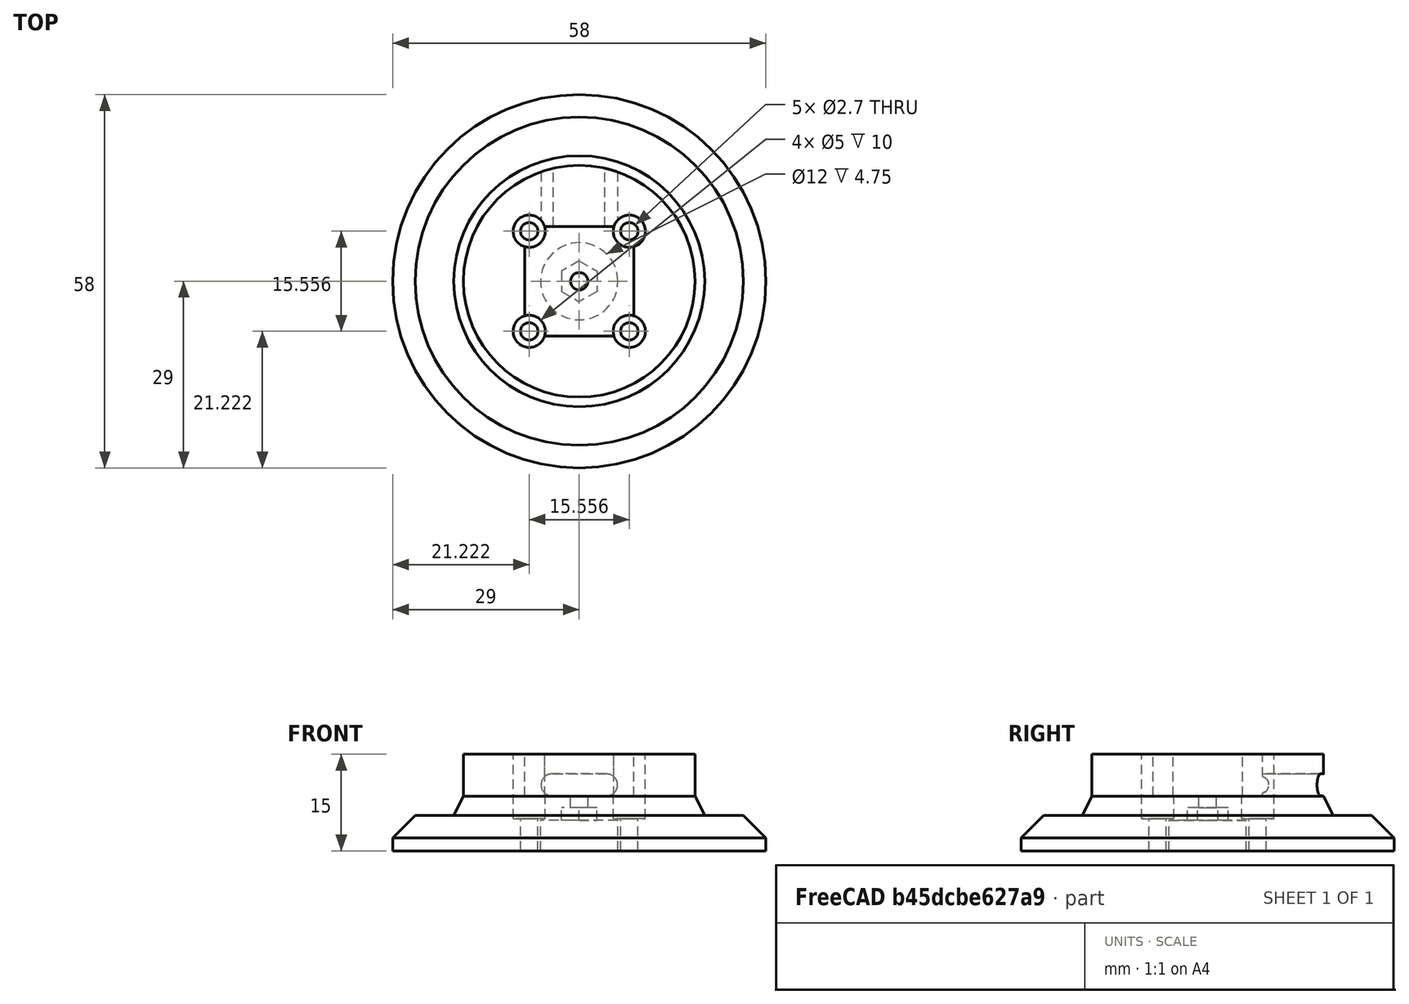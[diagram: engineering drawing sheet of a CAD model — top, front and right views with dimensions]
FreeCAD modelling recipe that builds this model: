
FCSTD DOCUMENT  (FreeCAD 0.14R2935 (Git))
Label: tendon_wheel_mx_18_29_mm
License: CC-BY 3.0
LicenseURL: http://creativecommons.org/licenses/by/3.0/
objects: Part::Cylinder×14, Part::MultiFuse×5, Part::Cut×3, Part::Box×2, Part::Cone×1, Part::Extrusion×1, Part::Mirroring×1, Part::Chamfer×1
note: 28 computed .brp shape members not serialized (recipe doc carries the construction recipe); baked Part::Feature solids carry a one-line shape summary decoded from their .brp

FEATURE [Part::Cylinder] Cylinder
  Angle = 360
  Height = 5.5
  Placement = pos=(0,0,-0.5) rot=(0,0,1;0rad)
  Radius = 29
FEATURE [Part::Cone] Cone
  Angle = 360
  Height = 4
  Placement = pos=(0,0,4) rot=(0,0,1;0rad)
  Radius1 = 20
  Radius2 = 18
FEATURE [Part::Cylinder] Cylinder001
  Angle = 360
  Height = 6.5
  Placement = pos=(0,0,8) rot=(0,0,1;0rad)
  Radius = 18
FEATURE [Part::MultiFuse] Fusion
  Shapes = -> [Cylinder,Cylinder001,Cone]
FEATURE [Part::Cylinder] Cylinder003  label="TopHole003"
  Angle = 360
  Height = 20
  Placement = pos=(-11,0,-3) rot=(0,0,1;0rad)
  Radius = 1.35
FEATURE [Part::Cylinder] Cylinder004  label="TopHole002"
  Angle = 360
  Height = 20
  Placement = pos=(0,-11,-3) rot=(0,0,1;0rad)
  Radius = 1.35
FEATURE [Part::Cylinder] Cylinder005  label="TopHole001"
  Angle = 360
  Height = 20
  Placement = pos=(11,0,-3) rot=(0,0,1;0rad)
  Radius = 1.35
FEATURE [Part::Cylinder] Cylinder006  label="TopHole"
  Angle = 360
  Height = 10
  Placement = pos=(0,11,-3) rot=(0,0,1;0rad)
  Radius = 1.35
FEATURE [Part::Cylinder] Cylinder007  label="TopHole004"
  Angle = 360
  Height = 20
  Placement = pos=(-11,0,2.5) rot=(0,0,1;0rad)
  Radius = 2.5
FEATURE [Part::Cylinder] Cylinder008  label="TopHole005"
  Angle = 360
  Height = 20
  Placement = pos=(11,0,2.5) rot=(0,0,1;0rad)
  Radius = 2.5
FEATURE [Part::Cylinder] Cylinder009  label="TopHole006"
  Angle = 360
  Height = 20
  Placement = pos=(0,11,2.5) rot=(0,0,1;0rad)
  Radius = 2.5
FEATURE [Part::Cylinder] Cylinder010  label="TopHole007"
  Angle = 360
  Height = 20
  Placement = pos=(0,-11,2.5) rot=(0,0,1;0rad)
  Radius = 2.5
FEATURE [Part::MultiFuse] Fusion001
  Placement = pos=(0,0,2) rot=(0,0,1;0.785397rad)
  Shapes = -> [Cylinder010,Cylinder007,Cylinder005,Cylinder003,Cylinder009,Cylinder004,Cylinder008,Cylinder006]
FEATURE [Part::Cylinder] Cylinder012  label="Cylinder003"
  Angle = 360
  Height = 30
  Placement = pos=(-4.25,30,9.75) rot=(1,0,0;1.5708rad)
  Radius = 1.7
FEATURE [Part::Cylinder] Cylinder013  label="Cylinder004"
  Angle = 360
  Height = 20
  Placement = pos=(0,0,-5) rot=(0,0,1;0rad)
  Radius = 1.35
FEATURE [Part::Box] Box  label="Cube"
  Height = 8
  Length = 17
  Placement = pos=(-8.5,-8.5,8) rot=(0,0,1;0rad)
  Width = 17
FEATURE [Part::Extrusion] Extrude
  Dir = (0,0,2)
  Solid = true
FEATURE [Part::Mirroring] Part__Mirroring  label="Extrude (Mirror #1)"
  Base = (0,0,0)
  Normal = (1,0,0)
  Source = -> Extrude
FEATURE [Part::MultiFuse] Fusion002
  Placement = pos=(0,0,4.2) rot=(0,0,1;0rad)
  Shapes = -> [Part__Mirroring,Extrude]
FEATURE [Part::MultiFuse] Fusion003
  Shapes = -> [Fusion002,Fusion001,Cylinder012,Box,Cylinder013]
FEATURE [Part::Cut] Cut
  Base = -> Fusion
  Tool = -> Fusion003
FEATURE [Part::Cylinder] Cylinder014  label="Cylinder005"
  Angle = 360
  Height = 4.75
  Placement = pos=(0,0,-0.5) rot=(0,0,1;0rad)
  Radius = 6
FEATURE [Part::Cut] Cut001
  Base = -> Cut
  Tool = -> Cylinder014
FEATURE [Part::Cylinder] Cylinder015  label="Cylinder006"
  Angle = 360
  Height = 30
  Placement = pos=(4.25,30,9.75) rot=(1,0,0;1.5708rad)
  Radius = 1.7
FEATURE [Part::Box] Box001  label="Cube001"
  Height = 3.4
  Length = 8
  Placement = pos=(-4,5,8.05) rot=(0,0,1;0rad)
  Width = 30
FEATURE [Part::MultiFuse] Fusion004
  Shapes = -> [Cylinder015,Box001]
FEATURE [Part::Cut] Cut002
  Base = -> Cut001
  Tool = -> Fusion004
FEATURE [Part::Chamfer] Chamfer
  Base = -> Cut002
  Edges = 1 edges r=3.5: [Edge1]
